# Revit family: M_Gate Valve_UNIVAL_GAV-0301 - 50-300 mm
name_source: partatom
category: Pipe Accessories
revit_build: Autodesk Revit 2016 (Build: 20150220_1215(x64)
units: mm (PartAtom-declared; Revit-internal decimal feet)

## family parameters
Always vertical = Yes
Cut with Voids When Loaded = No
OmniClass Number = 23.65.55.14.17
OmniClass Title = Adjusting/Controlling Valves for Liquid Services
Part Type = Valve - Breaks Into
Round Connector Dimension = Use Diameter
Shared = No
Work Plane-Based = No

## types (9) — shared parameters
Body Material = Cast iron
Colour = UNIVAL_Blue
Connection Type = Flanged
Description = Gate valve
Description TR = Sürgülü vana
Disc Material = Elastomer coated
Gasket Material = EPDM
K Coefficient Table = Gate Valve Flanged
Loss Method = K Coefficient from Table
Manufacturer = Giacomini Unival
Giacomini Unival
Giacomini Unival
Max. Working Temperature = 120°C
Pressure Rating = PN16 / PN25
URL = http://www.unival.com.tr

## per-type parameters (varying)
| type | Body_r1 | Body_r2 | Body_y1 | Body_y2 | C | Connection_r | D | DN | Flange | Flange_w | H | L | L1 | Model | Shaft_D | Shaft_L | WheelBed_D | WheelBed_L | WheelCenter_r | WheelProfile_w | Wheel_D |
| DN50 | 50 mm  [stored 0.164042 ft] | 30 mm  [stored 0.0984252 ft] | 65 mm  [stored 0.213255 ft] | 38 mm  [stored 0.124672 ft] | 160 mm | 25 mm  [stored 0.082021 ft] | 165 mm | 50 mm | M_Flange - 15-450 mm : DN50 | 17 mm  [stored 0.0557743 ft] | 197 mm | 150 mm | 116 mm | GAV-0301X050 | 8 mm  [stored 0.0262467 ft] | 15 mm  [stored 0.0492126 ft] | 20 mm  [stored 0.0656168 ft] | 25 mm  [stored 0.082021 ft] | 75 mm | 8 mm  [stored 0.0262467 ft] | 10 mm  [stored 0.0328084 ft] |
| DN65 | 57 mm | 34 mm  [stored 0.111549 ft] | 73 mm | 43 mm  [stored 0.141076 ft] | 200 mm | 33 mm  [stored 0.108268 ft] | 185 mm | 65 mm | M_Flange - 15-450 mm : DN65 | 17 mm  [stored 0.0557743 ft] | 228 mm | 170 mm | 136 mm | GAV-0301X065 | 9 mm  [stored 0.0295276 ft] | 17 mm  [stored 0.0557743 ft] | 23 mm  [stored 0.0754593 ft] | 28 mm  [stored 0.0918635 ft] | 94 mm | 9 mm  [stored 0.0295276 ft] | 11 mm  [stored 0.0360892 ft] |
| DN80 | 60 mm  [stored 0.19685 ft] | 36 mm  [stored 0.11811 ft] | 80 mm | 45 mm  [stored 0.147638 ft] | 200 mm | 40 mm  [stored 0.131234 ft] | 200 mm | 80 mm | M_Flange - 15-450 mm : DN80 | 17 mm  [stored 0.0557743 ft] | 254 mm | 180 mm | 146 mm | GAV-0301X080 | 10 mm  [stored 0.0328084 ft] | 18 mm  [stored 0.0590551 ft] | 24 mm  [stored 0.0787402 ft] | 30 mm  [stored 0.0984252 ft] | 94 mm | 10 mm  [stored 0.0328084 ft] | 12 mm  [stored 0.0393701 ft] |
| DN100 | 63 mm  [stored 0.206693 ft] | 38 mm  [stored 0.124672 ft] | 90 mm | 48 mm  [stored 0.15748 ft] | 200 mm | 50 mm  [stored 0.164042 ft] | 220 mm | 100 mm | M_Flange - 15-450 mm : DN100 | 17 mm  [stored 0.0557743 ft] | 281 mm | 190 mm | 156 mm | GAV-0301X100 | 10 mm  [stored 0.0328084 ft] | 19 mm | 25 mm  [stored 0.082021 ft] | 32 mm | 94 mm | 10 mm  [stored 0.0328084 ft] | 13 mm  [stored 0.0426509 ft] |
| DN125 | 67 mm | 40 mm  [stored 0.131234 ft] | 103 mm | 50 mm  [stored 0.164042 ft] | 250 mm | 63 mm  [stored 0.206693 ft] | 250 mm | 125 mm | M_Flange - 15-450 mm : DN125 | 17 mm  [stored 0.0557743 ft] | 340 mm | 200 mm | 166 mm | GAV-0301X125 | 11 mm  [stored 0.0360892 ft] | 20 mm  [stored 0.0656168 ft] | 27 mm  [stored 0.0885827 ft] | 33 mm  [stored 0.108268 ft] | 118 mm | 11 mm  [stored 0.0360892 ft] | 13 mm  [stored 0.0426509 ft] |
| DN150 | 70 mm | 42 mm  [stored 0.137795 ft] | 115 mm | 53 mm  [stored 0.173885 ft] | 250 mm | 75 mm | 285 mm | 150 mm | M_Flange - 15-450 mm : DN150 | 17 mm  [stored 0.0557743 ft] | 378 mm | 210 mm | 176 mm | GAV-0301X150 | 11 mm  [stored 0.0360892 ft] | 21 mm  [stored 0.0688976 ft] | 28 mm  [stored 0.0918635 ft] | 35 mm  [stored 0.114829 ft] | 118 mm | 11 mm  [stored 0.0360892 ft] | 14 mm  [stored 0.0459318 ft] |
| DN200 | 77 mm | 46 mm  [stored 0.150919 ft] | 140 mm | 58 mm  [stored 0.190289 ft] | 320 mm | 100 mm | 340 mm | 200 mm | M_Flange - 15-450 mm : DN200 | 18 mm  [stored 0.0590551 ft] | 460 mm | 230 mm | 194 mm | GAV-0301X200 | 12 mm  [stored 0.0393701 ft] | 23 mm  [stored 0.0754593 ft] | 31 mm | 38 mm  [stored 0.124672 ft] | 152 mm | 12 mm  [stored 0.0393701 ft] | 15 mm  [stored 0.0492126 ft] |
| DN250 | 83 mm | 50 mm  [stored 0.164042 ft] | 165 mm | 63 mm  [stored 0.206693 ft] | 366 mm | 125 mm | 400 mm | 250 mm | M_Flange - 15-450 mm : DN250 | 20 mm  [stored 0.0656168 ft] | 563 mm | 250 mm | 210 mm | GAV-0301X250 | 13 mm  [stored 0.0426509 ft] | 25 mm  [stored 0.082021 ft] | 33 mm  [stored 0.108268 ft] | 42 mm  [stored 0.137795 ft] | 175 mm | 13 mm  [stored 0.0426509 ft] | 17 mm  [stored 0.0557743 ft] |
| DN300 | 90 mm | 54 mm  [stored 0.177165 ft] | 190 mm | 68 mm | 366 mm | 150 mm | 455 mm | 300 mm | M_Flange - 15-450 mm : DN300 | 23 mm  [stored 0.0754593 ft] | 643 mm | 270 mm | 225 mm | GAV-0301X300 | 14 mm  [stored 0.0459318 ft] | 27 mm  [stored 0.0885827 ft] | 36 mm  [stored 0.11811 ft] | 45 mm  [stored 0.147638 ft] | 174 mm | 14 mm  [stored 0.0459318 ft] | 18 mm  [stored 0.0590551 ft] |

note: [stored X ft] marks values corroborated as IEEE doubles in the binary element streams (Revit-internal decimal feet)

## geometry (parser evidence)
native form markers: Sweep x5
no freeform markers — native parametric forms only
